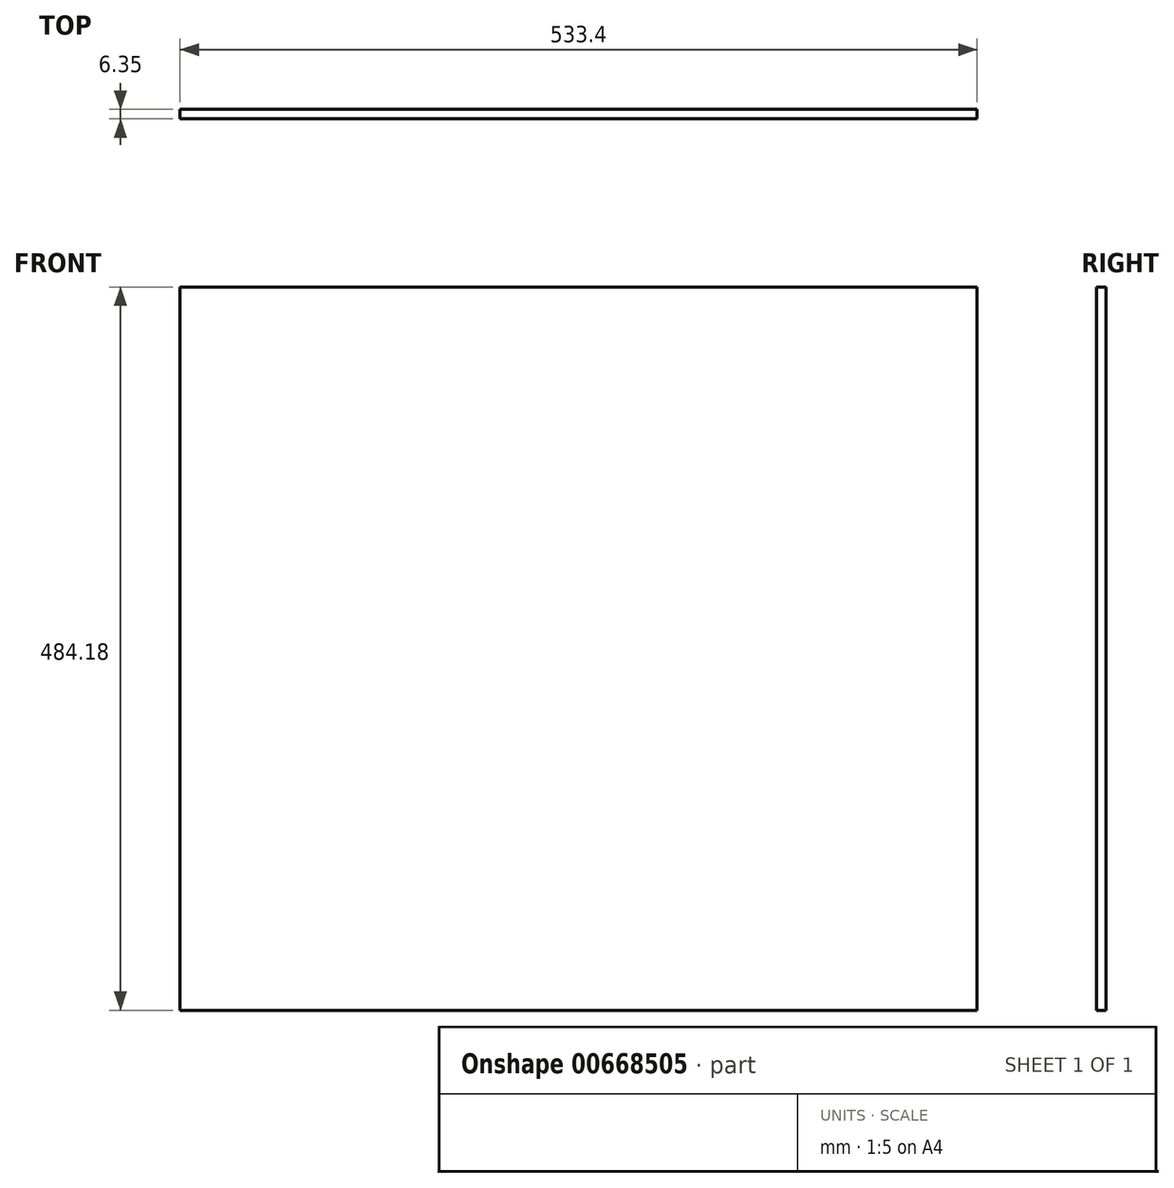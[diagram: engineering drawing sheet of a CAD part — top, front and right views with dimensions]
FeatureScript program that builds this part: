
annotation { "Feature Type Name" : "Feature", "Feature Type Description" : "" }
export const myFeature = defineFeature(function(context is Context, id is Id, definition is map)
    precondition{}
    {
        {
            var Q0;
            Q0=qCreatedBy(makeId("Front.planeOp"),FACE);
            var sketch = newSketch(context, id + "F0", { "sketchPlane" : qUnion([Q0])});
            skLineSegment(sketch, "E0.bottom", {"start": v(-266.7, -242.1) * mm, "end": v(266.7, -242.1) * mm});
            skLineSegment(sketch, "E0.top", {"start": v(-266.7, 242.1) * mm, "end": v(266.7, 242.1) * mm});
            skLineSegment(sketch, "E0.left", {"start": v(-266.7, -242.1) * mm, "end": v(-266.7, 242.1) * mm});
            skLineSegment(sketch, "E0.right", {"start": v(266.7, -242.1) * mm, "end": v(266.7, 242.1) * mm});
            skPoint(sketch, "E0.middle", {"position": v(0, 0) * mm});
            skSolve(sketch);
        }
        {
            var Q0;
            Q0=makeQuery(id+"F0.imprint","IMPRINT",FACE,{"disambiguationData":[TD([[makeQuery(id+"F0.imprint","IMPRINT",EDGE,{"derivedFrom":sQuery(id+"F0.wireOp",EDGE,"E0.bottom")}),1.0]])]});
            extrude(context, id + "F1", {"entities" : qUnion([Q0]), "depth" : 6.35 * mm, "offsetDistance" : 25.4 * mm});
        }
    });
